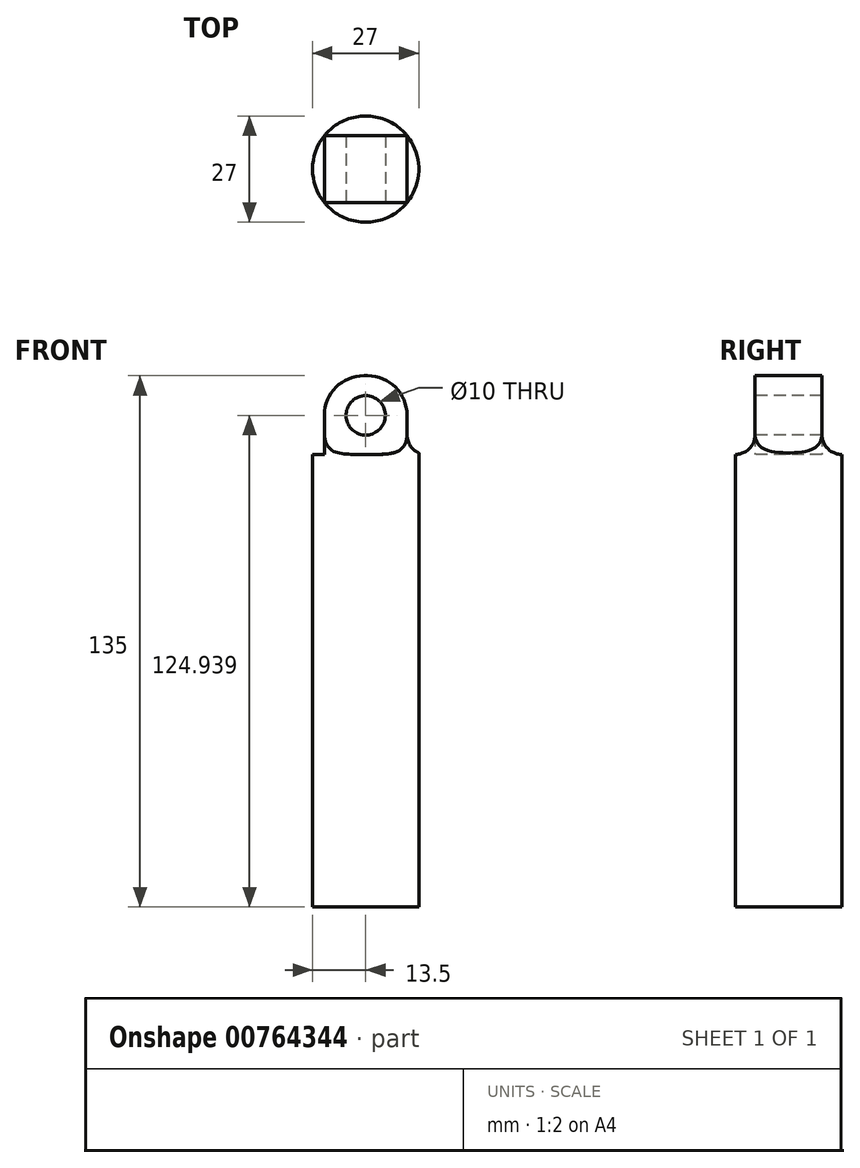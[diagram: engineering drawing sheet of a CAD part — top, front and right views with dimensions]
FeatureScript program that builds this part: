
annotation { "Feature Type Name" : "Feature", "Feature Type Description" : "" }
export const myFeature = defineFeature(function(context is Context, id is Id, definition is map)
    precondition{}
    {
        {
            var Q0;
            Q0=qCreatedBy(makeId("Top.planeOp"),FACE);
            var sketch = newSketch(context, id + "F0", { "sketchPlane" : qUnion([Q0])});
            skCircle(sketch, "E0", {"center": v(0, 0) * mm, "radius": 13.5 * mm});
            skSolve(sketch);
        }
        {
            var Q0;
            Q0 = qSketchRegion(id + "F0", true);
            extrude(context, id + "F1", {"entities" : qUnion([Q0]), "depth" : 115 * mm, "offsetDistance" : 25 * mm});
        }
        {
            var Q0;
            Q0=makeQuery(id+"F1.opExtrude","CAP_FACE",FACE,{"disambiguationData":[OSD([sQuery(id+"F0.wireOp",EDGE,"E0")])],"isStart":false});
            var sketch = newSketch(context, id + "F2", { "sketchPlane" : qUnion([Q0])});
            skLineSegment(sketch, "E1.bottom", {"start": v(-10.49, -8.5) * mm, "end": v(10.49, -8.5) * mm});
            skLineSegment(sketch, "E1.top", {"start": v(-10.49, 8.5) * mm, "end": v(10.49, 8.5) * mm});
            skLineSegment(sketch, "E1.left", {"start": v(-10.49, 8.5) * mm, "end": v(-10.49, -8.5) * mm});
            skLineSegment(sketch, "E1.right", {"start": v(10.49, 8.5) * mm, "end": v(10.49, -8.5) * mm});
            skPoint(sketch, "E1.middle", {"position": v(0, 0) * mm});
            skSolve(sketch);
        }
        {
            var Q0;
            Q0 = qSketchRegion(id + "F2", true);
            extrude(context, id + "F3", {"entities" : qUnion([Q0]), "operationType" : NewBodyOperationType.ADD, "depth" : 20 * mm, "offsetDistance" : 25 * mm});
        }
        {
            var Q0;
            Q0=makeQuery(id+"F3.opExtrude","SWEPT_FACE",FACE,{"disambiguationData":[OSD([sQuery(id+"F2.wireOp",EDGE,"E1.bottom")])]});
            var sketch = newSketch(context, id + "F4", { "sketchPlane" : qUnion([Q0])});
            skCircle(sketch, "E2", {"center": v(0, 124.94) * mm, "radius": 5 * mm});
            skSolve(sketch);
        }
        {
            var Q0;
            Q0 = qSketchRegion(id + "F4", true);
            extrude(context, id + "F5", {"entities" : qUnion([Q0]), "operationType" : NewBodyOperationType.REMOVE, "oppositeDirection" : true, "depth" : 25 * mm, "offsetDistance" : 25 * mm});
        }
        {
            var Q0;
            Q0=makeQuery(id+"F3.opExtrude","CAP_EDGE",EDGE,{"disambiguationData":[OSD([sQuery(id+"F2.wireOp",EDGE,"E1.right")])],"isStart":false});
            var Q1;
            Q1=makeQuery(id+"F3.opExtrude","CAP_EDGE",EDGE,{"disambiguationData":[OSD([sQuery(id+"F2.wireOp",EDGE,"E1.left")])],"isStart":false});
            fillet(context, id + "F6", {"entities" : qUnion([Q0, Q1]), "radius" : 10 * mm, "tangentPropagation" : true, "allowEdgeOverflow" : false});
        }
        {
            var Q0;
            Q0=makeQuery(id+"F3.opExtrude","CAP_EDGE",EDGE,{"disambiguationData":[OSD([sQuery(id+"F2.wireOp",EDGE,"E1.bottom")])],"isStart":true});
            var Q1;
            Q1=makeQuery(id+"F3.opExtrude","CAP_EDGE",EDGE,{"disambiguationData":[OSD([sQuery(id+"F2.wireOp",EDGE,"E1.top")])],"isStart":true});
            fillet(context, id + "F7", {"entities" : qUnion([Q0, Q1]), "radius" : 5 * mm, "tangentPropagation" : true, "allowEdgeOverflow" : false});
        }
        {
            var Q0;
            Q0=makeQuery(id+"F3.opExtrude","CAP_EDGE",EDGE,{"disambiguationData":[OSD([sQuery(id+"F2.wireOp",EDGE,"E1.right")])],"isStart":true});
            var Q1;
            Q1=makeQuery(id+"F3.opExtrude","CAP_EDGE",EDGE,{"disambiguationData":[OSD([sQuery(id+"F2.wireOp",EDGE,"E1.left")])],"isStart":true});
            fillet(context, id + "F8", {"entities" : qUnion([Q0, Q1]), "radius" : 5 * mm, "tangentPropagation" : true, "allowEdgeOverflow" : false});
        }
    });
